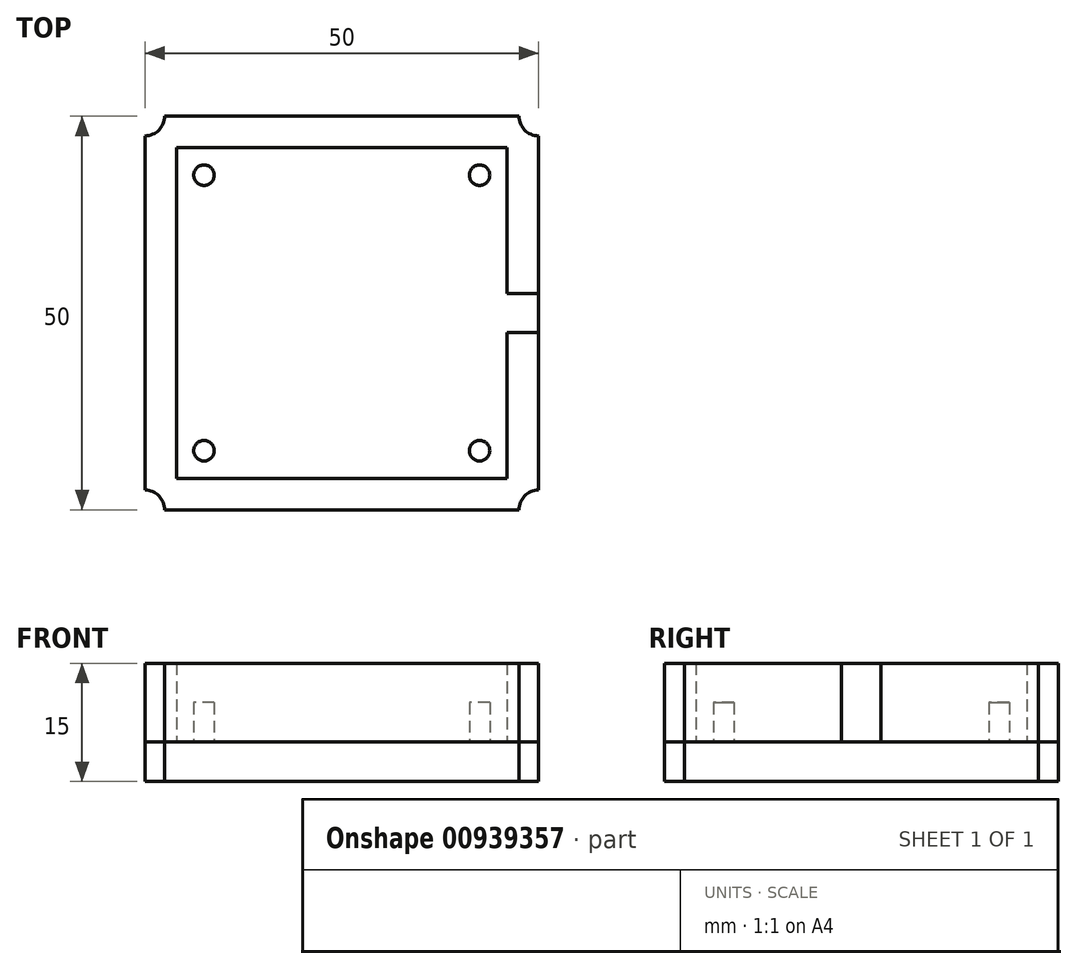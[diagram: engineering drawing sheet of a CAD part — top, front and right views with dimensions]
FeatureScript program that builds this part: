
annotation { "Feature Type Name" : "Feature", "Feature Type Description" : "" }
export const myFeature = defineFeature(function(context is Context, id is Id, definition is map)
    precondition{}
    {
        {
            var Q0;
            Q0=qCreatedBy(makeId("Top.planeOp"),FACE);
            var sketch = newSketch(context, id + "F0", { "sketchPlane" : qUnion([Q0])});
            skLineSegment(sketch, "E0.bottom", {"start": v(22.5, 25) * mm, "end": v(-22.5, 25) * mm});
            skLineSegment(sketch, "E0.top", {"start": v(22.5, -25) * mm, "end": v(-22.5, -25) * mm});
            skLineSegment(sketch, "E0.left", {"start": v(25, 22.5) * mm, "end": v(25, 2.5) * mm});
            skLineSegment(sketch, "E0.right", {"start": v(-25, 22.5) * mm, "end": v(-25, -22.5) * mm});
            skPoint(sketch, "E0.middle", {"position": v(0, 0) * mm});
            skLineSegment(sketch, "E1.bottom", {"start": v(21, 21) * mm, "end": v(-21, 21) * mm});
            skLineSegment(sketch, "E1.top", {"start": v(21, -21) * mm, "end": v(-21, -21) * mm});
            skLineSegment(sketch, "E1.left", {"start": v(21, 21) * mm, "end": v(21, 2.5) * mm});
            skLineSegment(sketch, "E1.right", {"start": v(-21, 21) * mm, "end": v(-21, -21) * mm});
            skCircle(sketch, "E2", {"center": v(17.5, 17.5) * mm, "radius": 1.3 * mm});
            skCircle(sketch, "E3", {"center": v(-17.5, 17.5) * mm, "radius": 1.3 * mm});
            skCircle(sketch, "E4", {"center": v(-17.5, -17.5) * mm, "radius": 1.3 * mm});
            skCircle(sketch, "E5", {"center": v(17.5, -17.5) * mm, "radius": 1.3 * mm});
            skLineSegment(sketch, "E6.bottom", {"start": v(25, 2.5) * mm, "end": v(21, 2.5) * mm});
            skLineSegment(sketch, "E6.top", {"start": v(25, -2.5) * mm, "end": v(21, -2.5) * mm});
            skLineSegment(sketch, "E7.trimOffspring", {"start": v(21, -2.5) * mm, "end": v(21, -21) * mm});
            skLineSegment(sketch, "E8.trimOffspring", {"start": v(25, -2.5) * mm, "end": v(25, -22.5) * mm});
            skArc(sketch, "E9", {"start": v(-25, 22.5) * mm, "mid": v(-23.23, 23.23) * mm, "end": v(-22.5, 25) * mm});
            skArc(sketch, "E10", {"start": v(22.5, 25) * mm, "mid": v(23.23, 23.23) * mm, "end": v(25, 22.5) * mm});
            skArc(sketch, "E11", {"start": v(25, -22.5) * mm, "mid": v(23.23, -23.23) * mm, "end": v(22.5, -25) * mm});
            skArc(sketch, "E12", {"start": v(-22.5, -25) * mm, "mid": v(-23.23, -23.23) * mm, "end": v(-25, -22.5) * mm});
            skLineSegment(sketch, "E13", {"start": v(25, 2.5) * mm, "end": v(25, -2.5) * mm});
            skSolve(sketch);
        }
        {
            var Q0;
            Q0=makeQuery(id+"F0.imprint","IMPRINT",FACE,{"disambiguationData":[TD([[makeQuery(id+"F0.imprint","IMPRINT",EDGE,{"derivedFrom":sQuery(id+"F0.wireOp",EDGE,"E1.bottom")}),-1.0]])]});
            var Q1;
            Q1=makeQuery(id+"F0.imprint","IMPRINT",FACE,{"disambiguationData":[TD([[makeQuery(id+"F0.imprint","IMPRINT",EDGE,{"derivedFrom":sQuery(id+"F0.wireOp",EDGE,"E3")}),1.0]])]});
            var Q2;
            Q2=makeQuery(id+"F0.imprint","IMPRINT",FACE,{"disambiguationData":[TD([[makeQuery(id+"F0.imprint","IMPRINT",EDGE,{"derivedFrom":sQuery(id+"F0.wireOp",EDGE,"E4")}),1.0]])]});
            var Q3;
            Q3=makeQuery(id+"F0.imprint","IMPRINT",FACE,{"disambiguationData":[TD([[makeQuery(id+"F0.imprint","IMPRINT",EDGE,{"derivedFrom":sQuery(id+"F0.wireOp",EDGE,"E5")}),1.0]])]});
            var Q4;
            Q4=makeQuery(id+"F0.imprint","IMPRINT",FACE,{"disambiguationData":[TD([[makeQuery(id+"F0.imprint","IMPRINT",EDGE,{"derivedFrom":sQuery(id+"F0.wireOp",EDGE,"E2")}),1.0]])]});
            extrude(context, id + "F1", {"entities" : qUnion([Q0, Q1, Q2, Q3, Q4]), "depth" : 5 * mm, "offsetDistance" : 25 * mm});
        }
        {
            var Q0;
            Q0=makeQuery(id+"F0.imprint","IMPRINT",FACE,{"disambiguationData":[TD([[makeQuery(id+"F0.imprint","IMPRINT",EDGE,{"derivedFrom":sQuery(id+"F0.wireOp",EDGE,"E1.bottom")}),-1.0]])]});
            var sketch = newSketch(context, id + "F2", { "sketchPlane" : qUnion([Q0])});
            skLineSegment(sketch, "E14.bottom", {"start": v(22.5, -25) * mm, "end": v(-22.5, -25) * mm});
            skLineSegment(sketch, "E14.top", {"start": v(22.5, 25) * mm, "end": v(-22.5, 25) * mm});
            skLineSegment(sketch, "E14.left", {"start": v(25, -22.5) * mm, "end": v(25, 22.5) * mm});
            skLineSegment(sketch, "E14.right", {"start": v(-25, -22.5) * mm, "end": v(-25, 22.5) * mm});
            skPoint(sketch, "E14.middle", {"position": v(0, 0) * mm});
            skArc(sketch, "E15", {"start": v(-25, 22.5) * mm, "mid": v(-23.23, 23.23) * mm, "end": v(-22.5, 25) * mm});
            skArc(sketch, "E16", {"start": v(22.5, 25) * mm, "mid": v(23.23, 23.23) * mm, "end": v(25, 22.5) * mm});
            skArc(sketch, "E17", {"start": v(25, -22.5) * mm, "mid": v(23.23, -23.23) * mm, "end": v(22.5, -25) * mm});
            skArc(sketch, "E18", {"start": v(-22.5, -25) * mm, "mid": v(-23.23, -23.23) * mm, "end": v(-25, -22.5) * mm});
            skSolve(sketch);
        }
        {
            var Q0;
            Q0=makeQuery(id+"F2.imprint","IMPRINT",FACE,{"disambiguationData":[TD([[makeQuery(id+"F2.imprint","IMPRINT",EDGE,{"derivedFrom":sQuery(id+"F2.wireOp",EDGE,"E14.bottom")}),-1.0]])]});
            var Q1;
            Q1=makeQuery(id+"F2.imprint","IMPRINT",FACE,{"disambiguationData":[TD([[makeQuery(id+"F2.imprint","IMPRINT",EDGE,{"derivedFrom":makeQuery(id+"F0.imprint","IMPRINT",EDGE,{"derivedFrom":sQuery(id+"F0.wireOp",EDGE,"E1.bottom")})}),1.0]])]});
            extrude(context, id + "F3", {"entities" : qUnion([Q0, Q1]), "depth" : -5 * mm, "offsetDistance" : 25 * mm});
        }
        {
            var Q0;
            Q0=makeQuery(id+"F1.opExtrude","CAP_FACE",FACE,{"disambiguationData":[OSD([sQuery(id+"F0.wireOp",EDGE,"E1.bottom"),sQuery(id+"F0.wireOp",EDGE,"E1.top"),sQuery(id+"F0.wireOp",EDGE,"E1.left"),sQuery(id+"F0.wireOp",EDGE,"E1.right"),sQuery(id+"F0.wireOp",EDGE,"E6.bottom"),sQuery(id+"F0.wireOp",EDGE,"E6.top"),sQuery(id+"F0.wireOp",EDGE,"E7.trimOffspring"),sQuery(id+"F0.wireOp",EDGE,"E0.bottom"),sQuery(id+"F0.wireOp",EDGE,"E0.top"),sQuery(id+"F0.wireOp",EDGE,"E0.left"),sQuery(id+"F0.wireOp",EDGE,"E0.right"),sQuery(id+"F0.wireOp",EDGE,"E8.trimOffspring"),sQuery(id+"F0.wireOp",EDGE,"E9"),sQuery(id+"F0.wireOp",EDGE,"E10"),sQuery(id+"F0.wireOp",EDGE,"E11"),sQuery(id+"F0.wireOp",EDGE,"E12")])],"isStart":false});
            extrude(context, id + "F4", {"entities" : qUnion([Q0]), "operationType" : NewBodyOperationType.ADD, "depth" : 5 * mm, "offsetDistance" : 25 * mm});
        }
    });
